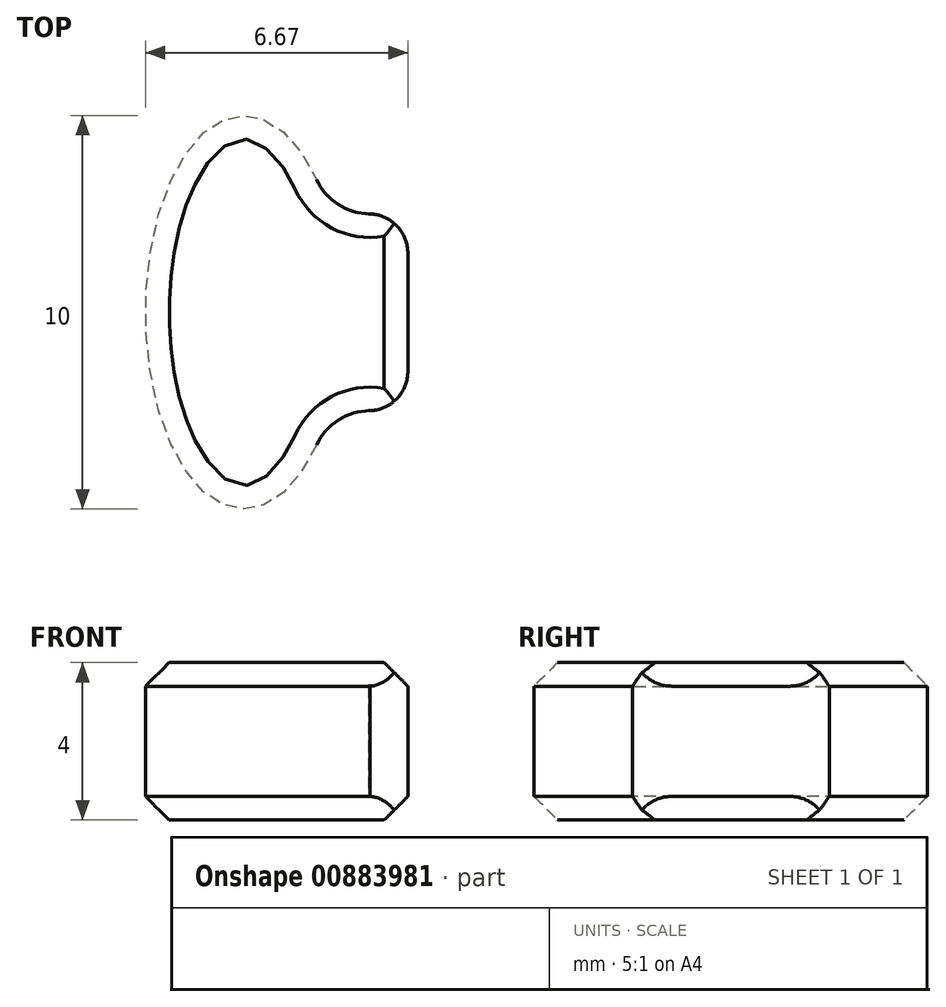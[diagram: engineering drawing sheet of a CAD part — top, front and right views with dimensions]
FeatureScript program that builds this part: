
annotation { "Feature Type Name" : "Feature", "Feature Type Description" : "" }
export const myFeature = defineFeature(function(context is Context, id is Id, definition is map)
    precondition{}
    {
        {
            var Q0;
            Q0=qCreatedBy(makeId("Top.planeOp"),FACE);
            var sketch = newSketch(context, id + "F0", { "sketchPlane" : qUnion([Q0])});
            skArc(sketch, "E0", {"start": v(12.38, 3.97) * mm, "mid": v(10.52, 7.64) * mm, "end": v(7.6, 10.55) * mm});
            skArc(sketch, "E1", {"start": v(9.5, 2.04) * mm, "mid": v(4.65, 0) * mm, "end": v(9.5, -2.04) * mm});
            skLineSegment(sketch, "E2", {"start": v(7.5, 0) * mm, "end": v(13, 0) * mm, "construction": true});
            skLineSegment(sketch, "E3", {"start": v(10.49, 1.8) * mm, "end": v(11.4, 2.08) * mm});
            skPoint(sketch, "E4.visualSharp", {"position": v(9.86, 1.6) * mm});
            skArc(sketch, "E4.filletArc", {"start": v(9.5, 2.04) * mm, "mid": v(9.96, 1.78) * mm, "end": v(10.49, 1.8) * mm});
            skPoint(sketch, "E5.visualSharp", {"position": v(12.76, 2.5) * mm});
            skArc(sketch, "E5.filletArc", {"start": v(11.4, 2.08) * mm, "mid": v(12.28, 2.82) * mm, "end": v(12.38, 3.97) * mm});
            skArc(sketch, "E6.MirrorCS", {"start": v(9.5, -2.04) * mm, "mid": v(9.96, -1.78) * mm, "end": v(10.49, -1.8) * mm});
            skLineSegment(sketch, "E7.MirrorCS", {"start": v(10.49, -1.8) * mm, "end": v(11.4, -2.08) * mm});
            skArc(sketch, "E8.MirrorCS", {"start": v(11.4, -2.08) * mm, "mid": v(12.28, -2.82) * mm, "end": v(12.38, -3.97) * mm});
            skPoint(sketch, "E9.orphan", {"position": v(9.86, -1.6) * mm});
            skPoint(sketch, "E10.orphan", {"position": v(12.76, -2.5) * mm});
            skPoint(sketch, "E11.1.0", {"position": v(1.56, 12.9) * mm});
            skPoint(sketch, "E11.1.1", {"position": v(6.32, 11.36) * mm});
            skPoint(sketch, "E11.1.2", {"position": v(1.52, 9.87) * mm});
            skLineSegment(sketch, "E11.1.3", {"start": v(2.32, 7.13) * mm, "end": v(4.02, 12.36) * mm, "construction": true});
            skArc(sketch, "E11.1.4", {"start": v(1, 9.66) * mm, "mid": v(1.44, 4.42) * mm, "end": v(4.87, 8.4) * mm});
            skArc(sketch, "E11.1.5", {"start": v(1.55, 11.48) * mm, "mid": v(1.12, 12.55) * mm, "end": v(0.05, 13) * mm});
            skArc(sketch, "E11.1.6", {"start": v(5.5, 10.2) * mm, "mid": v(6.47, 10.81) * mm, "end": v(7.6, 10.55) * mm});
            skPoint(sketch, "E11.1.7", {"position": v(4.57, 8.88) * mm});
            skArc(sketch, "E11.1.8", {"start": v(4.87, 8.4) * mm, "mid": v(4.77, 8.92) * mm, "end": v(4.95, 9.42) * mm});
            skArc(sketch, "E11.1.9", {"start": v(1, 9.66) * mm, "mid": v(1.39, 10.02) * mm, "end": v(1.53, 10.53) * mm});
            skLineSegment(sketch, "E11.1.10", {"start": v(1.53, 10.53) * mm, "end": v(1.55, 11.48) * mm});
            skLineSegment(sketch, "E11.1.11", {"start": v(4.95, 9.42) * mm, "end": v(5.5, 10.2) * mm});
            skPoint(sketch, "E11.2.1", {"position": v(-8.85, 9.52) * mm});
            skPoint(sketch, "E11.2.2", {"position": v(-8.92, 4.5) * mm});
            skLineSegment(sketch, "E11.2.3", {"start": v(-6.07, 4.4) * mm, "end": v(-10.52, 7.64) * mm, "construction": true});
            skArc(sketch, "E11.2.4", {"start": v(-8.88, 3.93) * mm, "mid": v(-3.76, 2.73) * mm, "end": v(-6.48, 7.23) * mm});
            skArc(sketch, "E11.2.6", {"start": v(-8, 8.38) * mm, "mid": v(-8.28, 9.5) * mm, "end": v(-7.68, 10.49) * mm});
            skPoint(sketch, "E11.2.7", {"position": v(-7.04, 7.09) * mm});
            skArc(sketch, "E11.2.8", {"start": v(-6.48, 7.23) * mm, "mid": v(-7.01, 7.3) * mm, "end": v(-7.43, 7.62) * mm});
            skArc(sketch, "E11.2.9", {"start": v(-8.88, 3.93) * mm, "mid": v(-9.1, 4.41) * mm, "end": v(-9.54, 4.71) * mm});
            skLineSegment(sketch, "E11.2.11", {"start": v(-7.43, 7.62) * mm, "end": v(-8, 8.38) * mm});
            skPoint(sketch, "E11.3.0", {"position": v(-8.85, -9.52) * mm});
            skPoint(sketch, "E11.3.2", {"position": v(-7.04, -7.09) * mm});
            skLineSegment(sketch, "E11.3.3", {"start": v(-6.07, -4.4) * mm, "end": v(-10.52, -7.64) * mm, "construction": true});
            skArc(sketch, "E11.3.4", {"start": v(-6.48, -7.23) * mm, "mid": v(-3.76, -2.73) * mm, "end": v(-8.88, -3.93) * mm});
            skArc(sketch, "E11.3.5", {"start": v(-8, -8.38) * mm, "mid": v(-8.28, -9.5) * mm, "end": v(-7.68, -10.49) * mm});
            skPoint(sketch, "E11.3.7", {"position": v(-8.92, -4.5) * mm});
            skArc(sketch, "E11.3.8", {"start": v(-8.88, -3.93) * mm, "mid": v(-9.1, -4.41) * mm, "end": v(-9.54, -4.71) * mm});
            skArc(sketch, "E11.3.9", {"start": v(-6.48, -7.23) * mm, "mid": v(-7.01, -7.3) * mm, "end": v(-7.43, -7.62) * mm});
            skLineSegment(sketch, "E11.3.10", {"start": v(-7.43, -7.62) * mm, "end": v(-8, -8.38) * mm});
            skPoint(sketch, "E11.4.0", {"position": v(6.32, -11.36) * mm});
            skPoint(sketch, "E11.4.1", {"position": v(1.56, -12.9) * mm});
            skPoint(sketch, "E11.4.2", {"position": v(4.57, -8.88) * mm});
            skLineSegment(sketch, "E11.4.3", {"start": v(2.32, -7.13) * mm, "end": v(4.02, -12.36) * mm, "construction": true});
            skArc(sketch, "E11.4.4", {"start": v(4.87, -8.4) * mm, "mid": v(1.44, -4.42) * mm, "end": v(1, -9.66) * mm});
            skArc(sketch, "E11.4.5", {"start": v(5.5, -10.2) * mm, "mid": v(6.47, -10.81) * mm, "end": v(7.6, -10.55) * mm});
            skArc(sketch, "E11.4.6", {"start": v(1.55, -11.48) * mm, "mid": v(1.12, -12.55) * mm, "end": v(0.05, -13) * mm});
            skPoint(sketch, "E11.4.7", {"position": v(1.52, -9.87) * mm});
            skArc(sketch, "E11.4.8", {"start": v(1, -9.66) * mm, "mid": v(1.39, -10.02) * mm, "end": v(1.53, -10.53) * mm});
            skArc(sketch, "E11.4.9", {"start": v(4.87, -8.4) * mm, "mid": v(4.77, -8.92) * mm, "end": v(4.95, -9.42) * mm});
            skLineSegment(sketch, "E11.4.10", {"start": v(4.95, -9.42) * mm, "end": v(5.5, -10.2) * mm});
            skLineSegment(sketch, "E11.4.11", {"start": v(1.53, -10.53) * mm, "end": v(1.55, -11.48) * mm});
            skArc(sketch, "E12.trimOffspring", {"start": v(0.05, 13) * mm, "mid": v(-4.02, 12.36) * mm, "end": v(-7.68, 10.49) * mm});
            skArc(sketch, "E13.trimOffspring", {"start": v(-7.68, -10.49) * mm, "mid": v(-4.02, -12.36) * mm, "end": v(0.05, -13) * mm});
            skArc(sketch, "E14.trimOffspring", {"start": v(7.6, -10.55) * mm, "mid": v(10.52, -7.64) * mm, "end": v(12.38, -3.97) * mm});
            skEllipticalArc(sketch, "E15", {});
            skFitSpline(sketch, "E16.0", {"points": [v(-18.64, -6.96) * mm, v(-18, -7.02) * mm, v(-17.36, -6.96) * mm, v(-16.76, -6.78) * mm, v(-16.23, -6.5) * mm, v(-15.6, -6.06) * mm, v(-14.98, -5.37) * mm, v(-14.42, -4.45) * mm, v(-14, -3.43) * mm, v(-13.71, -2.32) * mm, v(-13.54, -1.18) * mm, v(-13.48, 0) * mm, v(-13.54, 1.18) * mm, v(-13.71, 2.32) * mm, v(-14, 3.43) * mm, v(-14.42, 4.45) * mm, v(-14.98, 5.37) * mm, v(-15.6, 6.06) * mm, v(-16.23, 6.5) * mm, v(-16.76, 6.78) * mm, v(-17.36, 6.96) * mm, v(-18, 7.02) * mm, v(-18.64, 6.96) * mm, v(-19.24, 6.78) * mm, v(-19.77, 6.5) * mm, v(-20.4, 6.06) * mm, v(-21.02, 5.37) * mm, v(-21.58, 4.45) * mm, v(-22, 3.43) * mm, v(-22.29, 2.32) * mm, v(-22.46, 1.18) * mm, v(-22.52, 0) * mm, v(-22.46, -1.18) * mm, v(-22.29, -2.32) * mm, v(-22, -3.43) * mm, v(-21.58, -4.45) * mm, v(-21.02, -5.37) * mm, v(-20.4, -6.06) * mm, v(-19.77, -6.5) * mm, v(-19.24, -6.78) * mm, v(-18.64, -6.96) * mm, v(-18, -7.02) * mm, v(-17.36, -6.96) * mm]});
            skLineSegment(sketch, "E17", {"start": v(-9.54, -4.71) * mm, "end": v(-17.1, -6.87) * mm});
            skLineSegment(sketch, "E18", {"start": v(-9.54, 4.71) * mm, "end": v(-17.1, 6.87) * mm});
            skLineSegment(sketch, "E19", {"start": v(-14.83, 2.5) * mm, "end": v(-14.8, 2.5) * mm});
            skLineSegment(sketch, "E20", {"start": v(-13.83, 1.5) * mm, "end": v(-13.83, -1.5) * mm});
            skLineSegment(sketch, "E21", {"start": v(-14.8, -2.5) * mm, "end": v(-14.83, -2.5) * mm});
            skPoint(sketch, "E22.visualSharp", {"position": v(-15.83, 2.5) * mm});
            skArc(sketch, "E22.filletArc", {"start": v(-16.16, 3.38) * mm, "mid": v(-15.6, 2.74) * mm, "end": v(-14.8, 2.5) * mm});
            skPoint(sketch, "E23.visualSharp", {"position": v(-15.83, -2.5) * mm});
            skArc(sketch, "E23.filletArc", {"start": v(-14.8, -2.5) * mm, "mid": v(-15.6, -2.74) * mm, "end": v(-16.16, -3.38) * mm});
            skPoint(sketch, "E24.visualSharp", {"position": v(-13.83, 2.5) * mm});
            skArc(sketch, "E24.filletArc", {"start": v(-13.83, 1.5) * mm, "mid": v(-14.13, 2.2) * mm, "end": v(-14.83, 2.5) * mm});
            skPoint(sketch, "E25.visualSharp", {"position": v(-13.83, -2.5) * mm});
            skArc(sketch, "E25.filletArc", {"start": v(-14.83, -2.5) * mm, "mid": v(-14.13, -2.2) * mm, "end": v(-13.83, -1.5) * mm});
            const initialGuessF0  = {"E15": [-0.018, 0, 0, -1, 0.005, 0.0025, 2.311980366410433, 0.8296122871793601]};
            skSetInitialGuess(sketch, initialGuessF0);
            skSolve(sketch);
        }
        {
            var Q0;
            Q0 = qSketchRegion(id + "F0", true);
            extrude(context, id + "F1", {"entities" : qUnion([Q0]), "flatOperationType" : FlatOperationType.REMOVE, "depth" : 4 * mm, "offsetDistance" : 25 * mm, "domain" : OperationDomain.MODEL});
        }
        {
            var Q0;
            Q0=makeQuery(id+"F1.opExtrude","CAP_FACE",FACE,{"disambiguationData":[OSD([sQuery(id+"F0.wireOp",EDGE,"E0"),sQuery(id+"F0.wireOp",EDGE,"E1"),sQuery(id+"F0.wireOp",EDGE,"E3"),sQuery(id+"F0.wireOp",EDGE,"E4.filletArc"),sQuery(id+"F0.wireOp",EDGE,"E5.filletArc"),sQuery(id+"F0.wireOp",EDGE,"E6.MirrorCS"),sQuery(id+"F0.wireOp",EDGE,"E7.MirrorCS"),sQuery(id+"F0.wireOp",EDGE,"E8.MirrorCS"),sQuery(id+"F0.wireOp",EDGE,"E11.1.4"),sQuery(id+"F0.wireOp",EDGE,"E11.1.5"),sQuery(id+"F0.wireOp",EDGE,"E11.1.6"),sQuery(id+"F0.wireOp",EDGE,"E11.1.8"),sQuery(id+"F0.wireOp",EDGE,"E11.1.9"),sQuery(id+"F0.wireOp",EDGE,"E11.1.10"),sQuery(id+"F0.wireOp",EDGE,"E11.1.11"),sQuery(id+"F0.wireOp",EDGE,"E11.2.4"),sQuery(id+"F0.wireOp",EDGE,"E11.2.6"),sQuery(id+"F0.wireOp",EDGE,"E11.2.8"),sQuery(id+"F0.wireOp",EDGE,"E11.2.9"),sQuery(id+"F0.wireOp",EDGE,"E11.2.11"),sQuery(id+"F0.wireOp",EDGE,"E11.3.4"),sQuery(id+"F0.wireOp",EDGE,"E11.3.5"),sQuery(id+"F0.wireOp",EDGE,"E11.3.8"),sQuery(id+"F0.wireOp",EDGE,"E11.3.9"),sQuery(id+"F0.wireOp",EDGE,"E11.3.10"),sQuery(id+"F0.wireOp",EDGE,"E11.4.4"),sQuery(id+"F0.wireOp",EDGE,"E11.4.5"),sQuery(id+"F0.wireOp",EDGE,"E11.4.6"),sQuery(id+"F0.wireOp",EDGE,"E11.4.8"),sQuery(id+"F0.wireOp",EDGE,"E11.4.9"),sQuery(id+"F0.wireOp",EDGE,"E11.4.10"),sQuery(id+"F0.wireOp",EDGE,"E11.4.11"),sQuery(id+"F0.wireOp",EDGE,"E12.trimOffspring"),sQuery(id+"F0.wireOp",EDGE,"E13.trimOffspring"),sQuery(id+"F0.wireOp",EDGE,"E14.trimOffspring"),sQuery(id+"F0.wireOp",EDGE,"E15"),sQuery(id+"F0.wireOp",EDGE,"E16.0"),sQuery(id+"F0.wireOp",EDGE,"E17"),sQuery(id+"F0.wireOp",EDGE,"E18"),sQuery(id+"F0.wireOp",EDGE,"E20"),sQuery(id+"F0.wireOp",EDGE,"E22.filletArc"),sQuery(id+"F0.wireOp",EDGE,"E23.filletArc"),sQuery(id+"F0.wireOp",EDGE,"E24.filletArc"),sQuery(id+"F0.wireOp",EDGE,"E25.filletArc")])],"isStart":true});
            var Q1;
            Q1=makeQuery(id+"F1.opExtrude","CAP_FACE",FACE,{"disambiguationData":[OSD([sQuery(id+"F0.wireOp",EDGE,"E0"),sQuery(id+"F0.wireOp",EDGE,"E1"),sQuery(id+"F0.wireOp",EDGE,"E3"),sQuery(id+"F0.wireOp",EDGE,"E4.filletArc"),sQuery(id+"F0.wireOp",EDGE,"E5.filletArc"),sQuery(id+"F0.wireOp",EDGE,"E6.MirrorCS"),sQuery(id+"F0.wireOp",EDGE,"E7.MirrorCS"),sQuery(id+"F0.wireOp",EDGE,"E8.MirrorCS"),sQuery(id+"F0.wireOp",EDGE,"E11.1.4"),sQuery(id+"F0.wireOp",EDGE,"E11.1.5"),sQuery(id+"F0.wireOp",EDGE,"E11.1.6"),sQuery(id+"F0.wireOp",EDGE,"E11.1.8"),sQuery(id+"F0.wireOp",EDGE,"E11.1.9"),sQuery(id+"F0.wireOp",EDGE,"E11.1.10"),sQuery(id+"F0.wireOp",EDGE,"E11.1.11"),sQuery(id+"F0.wireOp",EDGE,"E11.2.4"),sQuery(id+"F0.wireOp",EDGE,"E11.2.6"),sQuery(id+"F0.wireOp",EDGE,"E11.2.8"),sQuery(id+"F0.wireOp",EDGE,"E11.2.9"),sQuery(id+"F0.wireOp",EDGE,"E11.2.11"),sQuery(id+"F0.wireOp",EDGE,"E11.3.4"),sQuery(id+"F0.wireOp",EDGE,"E11.3.5"),sQuery(id+"F0.wireOp",EDGE,"E11.3.8"),sQuery(id+"F0.wireOp",EDGE,"E11.3.9"),sQuery(id+"F0.wireOp",EDGE,"E11.3.10"),sQuery(id+"F0.wireOp",EDGE,"E11.4.4"),sQuery(id+"F0.wireOp",EDGE,"E11.4.5"),sQuery(id+"F0.wireOp",EDGE,"E11.4.6"),sQuery(id+"F0.wireOp",EDGE,"E11.4.8"),sQuery(id+"F0.wireOp",EDGE,"E11.4.9"),sQuery(id+"F0.wireOp",EDGE,"E11.4.10"),sQuery(id+"F0.wireOp",EDGE,"E11.4.11"),sQuery(id+"F0.wireOp",EDGE,"E12.trimOffspring"),sQuery(id+"F0.wireOp",EDGE,"E13.trimOffspring"),sQuery(id+"F0.wireOp",EDGE,"E14.trimOffspring"),sQuery(id+"F0.wireOp",EDGE,"E15"),sQuery(id+"F0.wireOp",EDGE,"E16.0"),sQuery(id+"F0.wireOp",EDGE,"E17"),sQuery(id+"F0.wireOp",EDGE,"E18"),sQuery(id+"F0.wireOp",EDGE,"E20"),sQuery(id+"F0.wireOp",EDGE,"E22.filletArc"),sQuery(id+"F0.wireOp",EDGE,"E23.filletArc"),sQuery(id+"F0.wireOp",EDGE,"E24.filletArc"),sQuery(id+"F0.wireOp",EDGE,"E25.filletArc")])],"isStart":false});
            chamfer(context, id + "F2", {"entities" : qUnion([Q0, Q1]), "width" : .6 * mm, "tangentPropagation" : true});
        }
    });
